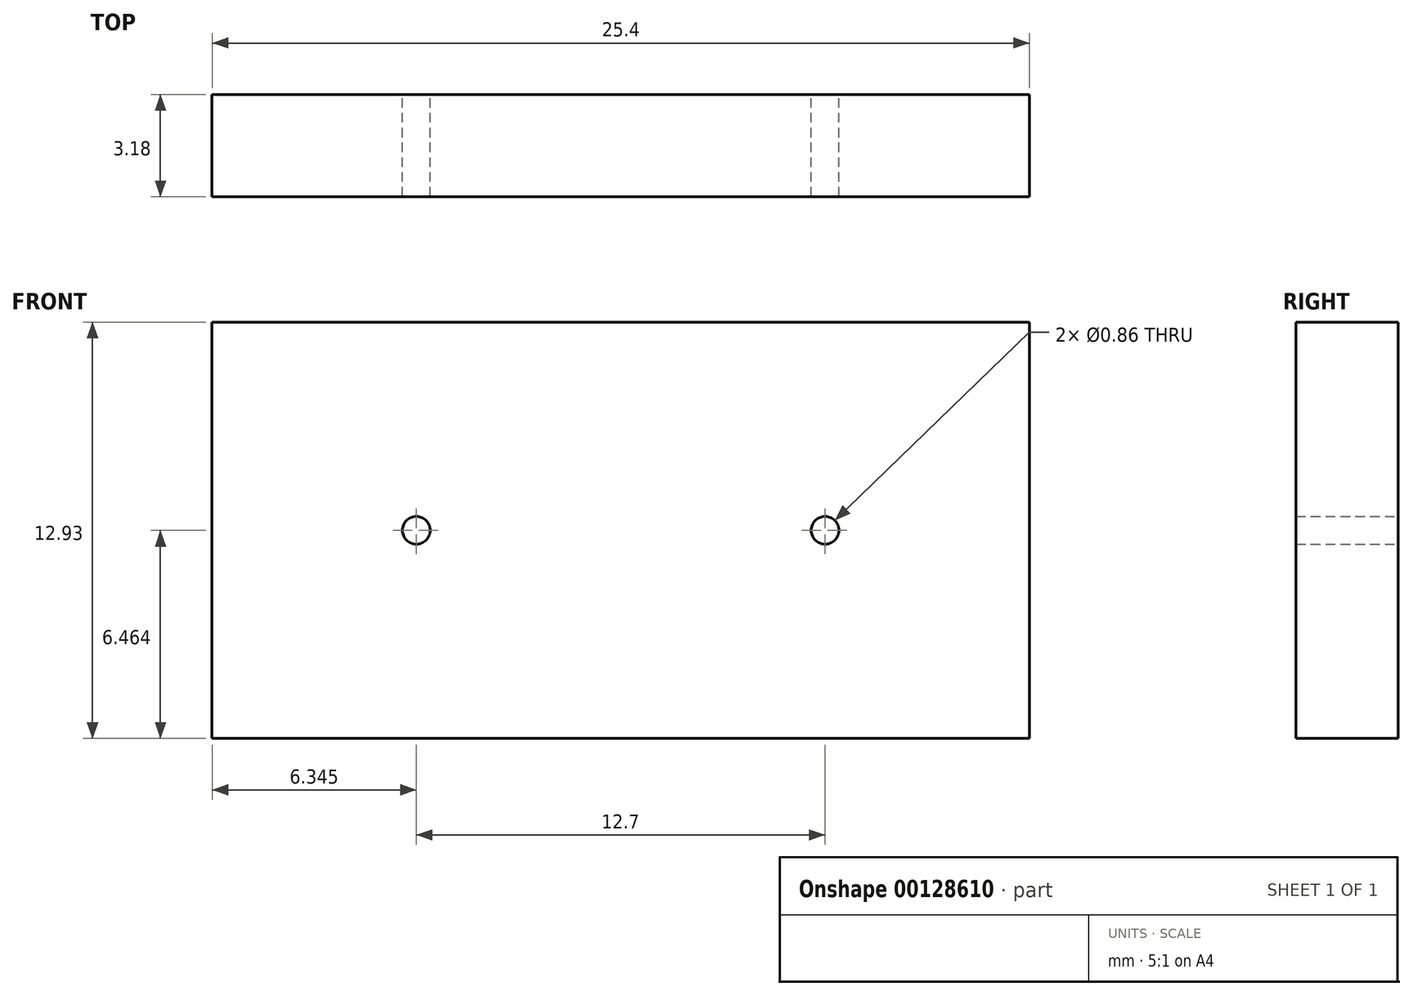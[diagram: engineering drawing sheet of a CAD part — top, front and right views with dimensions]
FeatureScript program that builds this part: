
annotation { "Feature Type Name" : "Feature", "Feature Type Description" : "" }
export const myFeature = defineFeature(function(context is Context, id is Id, definition is map)
    precondition{}
    {
        {
            var Q0;
            Q0=qCreatedBy(makeId("Front.planeOp"),FACE);
            var sketch = newSketch(context, id + "F0", { "sketchPlane" : qUnion([Q0])});
            skLineSegment(sketch, "E0.bottom", {"start": v(-25.13, 12.93) * mm, "end": v(0.27, 12.93) * mm});
            skLineSegment(sketch, "E0.top", {"start": v(-25.13, 0) * mm, "end": v(0.27, 0) * mm});
            skLineSegment(sketch, "E0.left", {"start": v(-25.13, 12.93) * mm, "end": v(-25.13, 0) * mm});
            skLineSegment(sketch, "E0.right", {"start": v(0.27, 12.93) * mm, "end": v(0.27, 0) * mm});
            skLineSegment(sketch, "E1", {"start": v(-12.43, 12.93) * mm, "end": v(-12.43, 0) * mm});
            skLineSegment(sketch, "E2", {"start": v(-12.43, 6.46) * mm, "end": v(0.27, 6.46) * mm});
            skLineSegment(sketch, "E3", {"start": v(-12.43, 6.46) * mm, "end": v(-25.13, 6.46) * mm});
            skLineSegment(sketch, "E4", {"start": v(-18.78, 6.46) * mm, "end": v(-18.78, 12.93) * mm});
            skLineSegment(sketch, "E5", {"start": v(-6.08, 6.46) * mm, "end": v(-6.08, 12.93) * mm});
            skCircle(sketch, "E6", {"center": v(-18.78, 6.46) * mm, "radius": 0.43 * mm});
            skCircle(sketch, "E7", {"center": v(-6.08, 6.46) * mm, "radius": 0.43 * mm});
            skSolve(sketch);
        }
        {
            var Q0;
            Q0=makeQuery(id+"F0.imprint","IMPRINT",FACE,{"disambiguationData":[TD([[makeQuery(id+"F0.imprint","IMPRINT",EDGE,{"derivedFrom":sQuery(id+"F0.wireOp",EDGE,"E0.bottom")}),-1.0]])]});
            var Q1;
            {var subQ5=sQuery(id+"F0.wireOp",EDGE,"E0.top");var subQ7=sQuery(id+"F0.wireOp",EDGE,"E0.left");var subQ8=makeQuery(id+"F0.imprint","INTERSECT",VERTEX,{"derivedFrom":[subQ5,subQ7]});Q1=makeQuery(id+"F0.imprint","IMPRINT",FACE,{"disambiguationData":[TD([[makeQuery(id+"F0.imprint","IMPRINT",EDGE,{"disambiguationData":[TD([[subQ8,-1.0]])],"derivedFrom":subQ5}),1.0]])]});}
            var Q2;
            {var subQ5=sQuery(id+"F0.wireOp",EDGE,"E0.right");var subQ6=sQuery(id+"F0.wireOp",EDGE,"E0.top");var subQ7=makeQuery(id+"F0.imprint","INTERSECT",VERTEX,{"derivedFrom":[subQ6,subQ5]});Q2=makeQuery(id+"F0.imprint","IMPRINT",FACE,{"disambiguationData":[TD([[makeQuery(id+"F0.imprint","IMPRINT",EDGE,{"disambiguationData":[TD([[subQ7,1.0]])],"derivedFrom":subQ6}),1.0]])]});}
            extrude(context, id + "F1", {"entities" : qUnion([Q0, Q1, Q2]), "depth" : 3.17 * mm});
        }
    });
